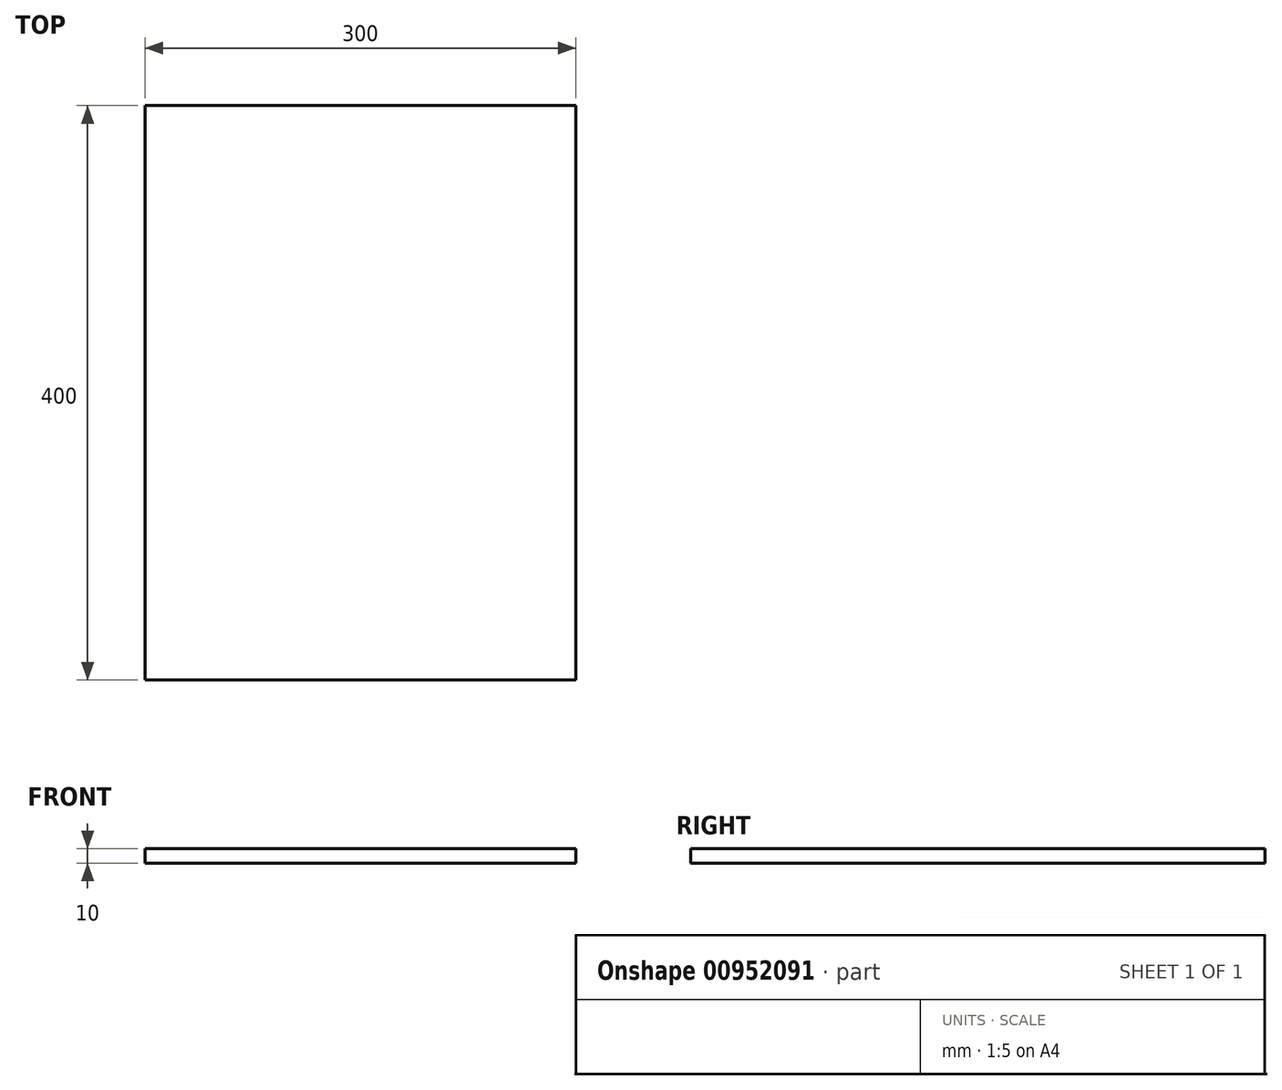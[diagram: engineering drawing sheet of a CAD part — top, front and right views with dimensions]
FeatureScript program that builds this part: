
annotation { "Feature Type Name" : "Feature", "Feature Type Description" : "" }
export const myFeature = defineFeature(function(context is Context, id is Id, definition is map)
    precondition{}
    {
        {
            var Q0;
            Q0=qCreatedBy(makeId("Top.planeOp"),FACE);
            var sketch = newSketch(context, id + "F0", { "sketchPlane" : qUnion([Q0])});
            skLineSegment(sketch, "E0.bottom", {"start": v(-150, 200) * mm, "end": v(150, 200) * mm});
            skLineSegment(sketch, "E0.top", {"start": v(-150, -200) * mm, "end": v(150, -200) * mm});
            skLineSegment(sketch, "E0.left", {"start": v(-150, 200) * mm, "end": v(-150, -200) * mm});
            skLineSegment(sketch, "E0.right", {"start": v(150, 200) * mm, "end": v(150, -200) * mm});
            skPoint(sketch, "E0.middle", {"position": v(0, 0) * mm});
            skSolve(sketch);
        }
        {
            var Q0;
            Q0 = qSketchRegion(id + "F0", true);
            extrude(context, id + "F1", {"entities" : qUnion([Q0]), "depth" : 10 * mm, "offsetDistance" : 25 * mm});
        }
    });
